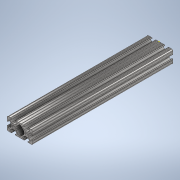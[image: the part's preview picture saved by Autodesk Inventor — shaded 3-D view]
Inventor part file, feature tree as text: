
AUTODESK INVENTOR PART (.ipt)
format: ipt  version: 2020 (Build 240168000, 168)  size: 343,552 bytes
history: native  units: in
note: dims shown in document units (in); Inventor stores cm internally (conversion verified against a paired STEP export)
features: sketch x2, extrude x1
ambient origin geometry x8: Origin, YZ Plane, XZ Plane, XY Plane, X Axis, Y Axis, Z Axis, Center Point
bodies: Solid1 (feature_tree)
feature tree (3):
  extrude  "Extrusion1"  [1 undecoded]
  sketch  "Sketch2"
  sketch  "Sketch1"  dims[d0=11.0in d1=0.0in]
note: 1 required parameter value undecoded (feature->parameter linkage not recoverable at this tier; creation-order binding heuristic only, values carry confidence <= 0.55)
